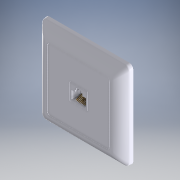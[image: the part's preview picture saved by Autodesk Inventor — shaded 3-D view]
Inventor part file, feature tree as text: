
AUTODESK INVENTOR PART (.ipt)
format: ipt  version: 2019.1 (Build 231200000, 200)  size: 2,302,464 bytes
history: native  units: mm
features: sketch x23, other x20, extrude x12, fillet x9, mirror x4, projected_geometry x4, loft x1, sweep x1, pattern_linear x1
ambient origin geometry x8: Origin, YZ Plane, XZ Plane, XY Plane, X Axis, Y Axis, Z Axis, Center Point
bodies: Body1 (feature_tree), Body2 (feature_tree)
feature tree (75):
  other  "Блоки"
  sketch  "Эскиз3"
  sketch  "Эскиз30"
  sketch  "3D эскиз1"
  loft  "korpus l"
  extrude  "lan 1"  Depth=11.5mm
  extrude  "lan 2"  Depth=4.0mm
  other  "РабПлоскость10"
  sketch  "Эскиз43"
  sketch  "3D эскиз2"
  extrude  "lan 3"  Depth=2.75mm
  extrude  "lan 4"  Depth=0.2mm
  extrude  "lan 5"  Depth=1.0mm
  extrude  "lan 6"  Depth=40.0mm
  extrude  "lan 7"  Depth=5.8mm
  mirror  "lan 8"
  sweep  "lan 9"
  mirror  "lan 10"
  pattern_linear  "lan 11"  Spacing1=6.0mm  [1 undecoded]
  fillet  "lan 12"  Radius=9.45mm
  extrude  "lan 13"  Depth=9.45mm
  fillet  "lan 14"  Radius=35.0mm
  fillet  "lan 15"  Radius=7.75mm
  fillet  "Сопряжение17"  Radius=20.0mm
  fillet  "Сопряжение18"  Radius=35.0mm
  extrude  "Выдавливание33"  Depth=4.9mm
  mirror  "Зеркальное отражение3"
  extrude  "Выдавливание34"  Depth=3.7mm
  extrude  "Выдавливание35"  Depth=35.0mm
  extrude  "Выдавливание36"  Depth=7.75mm
  fillet  "Сопряжение19"  Radius=4.9mm
  fillet  "Сопряжение20"  Radius=1.0mm
  fillet  "Сопряжение21"  Radius=2.0mm
  fillet  "Сопряжение22"  [1 undecoded]
  sketch  "Эскиз4"
  other  "Блок1"
  other  "Блок2"
  sketch  "Эскиз29"
  sketch  "Эскиз31"
  sketch  "Эскиз32"
  other  "РабПлоскость4"
  other  "korpus"
  other  "РабПлоскость8"
  sketch  "Эскиз40"
  sketch  "Эскиз41"
  other  "Картинка1"
  other  "РабПлоскость9"
  other  "lan"
  sketch  "Эскиз42"
  other  "РабПлоскость11"
  other  "9mm"
  mirror  "simetria"
  sketch  "Эскиз44"
  projected_geometry  "Спроецированная петля7"
  sketch  "Эскиз45"
  other  "РабПлоскость14"
  projected_geometry  "Спроецированная петля8"
  sketch  "Эскиз46"
  other  "РабПлоскость15"
  other  "РабПлоскость16"
  other  "РабПлоскость17"
  sketch  "Эскиз47"
  sketch  "Эскиз48"
  sketch  "Эскиз49"
  sketch  "Эскиз50"
  projected_geometry  "Спроецированная петля9"
  sketch  "Эскиз52"
  sketch  "Эскиз53"
  projected_geometry  "Спроецированная петля10"
  sketch  "Эскиз54"
  sketch  "Эскиз55"
  other  "Блок2:3"
  other  "Блок2:6"
  other  "Блок2:7"
  other  "Блок2:8"
note: 2 required parameter values undecoded (feature->parameter linkage not recoverable at this tier; creation-order binding heuristic only, values carry confidence <= 0.55)
